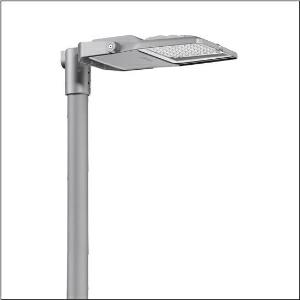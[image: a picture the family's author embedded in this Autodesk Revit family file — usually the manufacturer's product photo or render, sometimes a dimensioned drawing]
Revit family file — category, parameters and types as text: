
# Revit family: floodlight_fl_21_mini___pl64_5xa7776b2e3a_216f
name_source: partatom
category: Lighting Fixtures
units: mm (PartAtom-declared; Revit-internal decimal feet)

## family parameters
Cut with Voids When Loaded = No
Host = Face
Light Source = No
Part Type = Normal
Room Calculation Point = No
Round Connector Dimension = Use Diameter
Shared = No

## types (1)
- --- (1 x LED, 6010 lm, 45.7 W, 3000K)
    Apparent Load = 46 VA
    CIE Flux Codes = 28 80 98 100 100
    Color Rendering = 70
    Color Temperature = 3000K
    Default Elevation = 1800 mm
    Description = Floodlight FL 21 mini, floodlight, primary light control with lens, of PMMA, primary optical cover: protective disc, of toughened safety glass, transparent, light distribution: PL64, light emission: direct distribution, installation type: surface-mounted, LED, High Power LED, rated luminous flux: 6.010lm, luminous efficacy: 132lm/W, light colour: 730, colour temperature: 3000K, control: flexible luminous flux parameterisation, time-dependent luminous flux control, constant luminous flux control, overheat protection, pre-setting: logarithmic dimming characteristic, with terminal, 6-pole, mains connection: 220..240V, AC, 50/60Hz, start of lifetime: 46W, end of service life: 48W, reduction: 22W, luminaire housing, of diecast aluminium, powder-coated, Siteco® metallic grey (DB 702S), corrosivity category C5 mid according to DIN EN ISO 12944, sealing non-destructively replaceable, please order mast flange separately, mast bracket, of steel, galvanised, powder-coated, Siteco® metallic grey (DB 702S), Smart Interface below and above, protection rating (complete): IP66, insulation class (complete): insulation class II (safety insulation), certification: CE, ENEC, VDE, protection symbol: D, impact resistance: IK08, permissible operating ambient temperature: -40..+40°C, permissible operating ambient temperature for outdoor applications: -40..+50°C, standard: DIN EN 12944, LABS conformity tested according to VDMA 24364:2018-05, packaging unit: 1 piece

Light Distribution: PL64
    Height = 70 mm
    Lamp = 1 x LED
    Lamp Light Flux = 6010 lm
    Lamp Power = 45.7 W
    Lamp count = 1
    Length = 485 mm
    Luminous efficacy = 132 lm/W
    Manufacturer = Siteco
    ModVariant = No
    Model = 5XA7776B2E3A
    Number of Poles = 1
    OnlyDefault = Yes
    Power Factor = 1
    Product Name = Floodlight FL 21 mini | PL64
    Product group = floodlight | pylon annexe
    ProductGroupID = 6200
    Protection Class = Protection class II
    Protection Degree = IP 66
    RLX_Detail_Level = 1
    RLX_Emergency_Light_Flux = 0 lm
    RLX_Emergency_Type = 0
    RLX_Emergency_Type_DB = No
    RlxData = <blob elided: 100945 chars, md5=5387ae33>
    Socket = socket
    Standby Power = 0 W
    System Light Flux = 6010 lm
    System Power = 46 W
    Type Comments = factory setting: luminous flux: 100 % | dim-lin: 254 | 463 mA
    Type Image = l_1007125.jpg
    URL = http://relux.com
    VarID = @adj_135809
    Voltage = 0 V
    Weight = 0.00 kg
    Width = 337 mm

## geometry (parser evidence)
native form markers: Blend x4, Sweep x13
no freeform markers — native parametric forms only
